# Revit family: Guardrail_Kattsafe_AccessHatchKit
name_source: partatom
category: Specialty Equipment
units: mm (PartAtom-declared; Revit-internal decimal feet)

## family parameters
Always vertical = No
Cut with Voids When Loaded = No
Enable Cutting in Views = No
Maintain Annotation Orientation = No
OmniClass Number = 23.17.25.11
Part Type = Normal
Room Calculation Point = No
Round Connector Dimension = Use Diameter
Shared = Yes
Work Plane-Based = Yes

## types (2) — shared parameters
Assembly Code = E1090100
Description = Kattsafe guardrail systems are the preferred method of safe access across roofs and areas close to a fall edge. The system requires no specialist PPE, personnel or training to safely prevent a fall with a walkway to designate a safe path of access across the roof surface.
Export Type to IFC As = IfcRailing
IfcExportAs = IfcRailing
IfcExportType = GUARDRAIL
Manufacturer = Kattsafe®
ManufacturerOverallDepth = 1800 mm  [stored 5.90551 ft]
ManufacturerOverallHeight = 1100 mm
ManufacturerOverallWidth = 1800 mm  [stored 5.90551 ft]
ManufacturerURLProductSpecific = https://kattsafe.com.au
Material = Aluminum_Kattsafe_Satin
ModifiedIssue = 20240430 $
Type IFC Predefined Type = GUARDRAIL
URL = https://kattsafe.com.au
Uniclass2015Code = Pr_25_30_36_03
Uniclass2015Title = Aluminium handrails
Uniclass2015Version = Products v1.23
zero-valued in all types: Default Elevation

## per-type parameters (varying)
| type | ConcreteMount | ManufacturerSpecCode | MetalDeckMount | Model | Type Comments |
| Concrete Mount (GW394C) | Yes | GW394C | No | GW394C | Access Hatch Guardrail Kit - Concrete Mount |
| Metal Deck Mount (GW394D) | No | GW394D | Yes | GW394D | Access Hatch Guardrail Kit - Metal Deck Mount |

note: [stored X ft] marks values corroborated as IEEE doubles in the binary element streams (Revit-internal decimal feet)

## geometry (parser evidence)
native form markers: Sweep x4
no freeform markers — native parametric forms only
